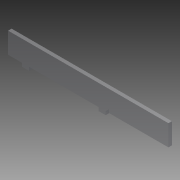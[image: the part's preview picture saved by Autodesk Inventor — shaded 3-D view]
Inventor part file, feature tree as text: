
AUTODESK INVENTOR PART (.ipt)
format: ipt  version: 2013 (Build 170138000, 138)  size: 80,896 bytes
history: native  units: in
note: dims shown in document units (in); Inventor stores cm internally (conversion verified against a paired STEP export)
features: extrude x1, sketch x1
ambient origin geometry x8: Origin, YZ Plane, XZ Plane, XY Plane, X Axis, Y Axis, Z Axis, Center Point
bodies: Solid1 (feature_tree)
feature tree (2):
  extrude  "Extrusion1"  Depth=1.0in
  sketch  "Sketch1"  dims[d0=1.5in d1=1.0in d3=0.25in d4=0.5in d5=5.0in d6=0.5in d7=11.5in d8=0.25in d9=0.0in]
